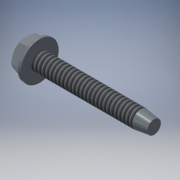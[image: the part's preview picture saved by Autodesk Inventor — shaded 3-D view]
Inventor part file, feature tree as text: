
AUTODESK INVENTOR PART (.ipt)
format: ipt  version: 2017.1 (Build 211199000, 199)  size: 189,440 bytes
history: native  units: mm (DEFAULTED — no unit token found)
features: sketch x4, extrude x2, other x1, chamfer x1, plane x1
ambient origin geometry x8: Origin, YZ Plane, XZ Plane, XY Plane, X Axis, Y Axis, Z Axis, Center Point
bodies: Solid1 (feature_tree), Body (feature_tree)
feature tree (9):
  extrude  "Head"  Depth=0.7874mm
  other  "IDS_WORKPLANE{1}"
  extrude  "Indent"  TaperAngle=90.0deg  [1 undecoded]
  chamfer  "Chamfer1"  [1 undecoded]
  plane  "Work Plane3"
  sketch  "Sketch1"  dims[d1=0.7874mm d2=4.826mm]
  sketch  "Sketch2"  dims[d3=31.75mm d77=90.0deg]
  sketch  "Sketch3"  dims[d6=31.75mm]
  sketch  "Sketch4"  dims[d7=0.0mm d10=0.0mm d11=7.9248mm d12=3.048mm d13=0.0mm d14=0.0mm d15=6.33984mm d16=0.3048mm d17=0.0mm d92=90.0deg d19=0.5334mm d20=3.7084mm d21=7.9248mm d22=10.5156mm d23=6.863078mm d98=45.0deg d99=0.0mm d100=0.0mm]
note: 2 required parameter values undecoded (feature->parameter linkage not recoverable at this tier; creation-order binding heuristic only, values carry confidence <= 0.55)
